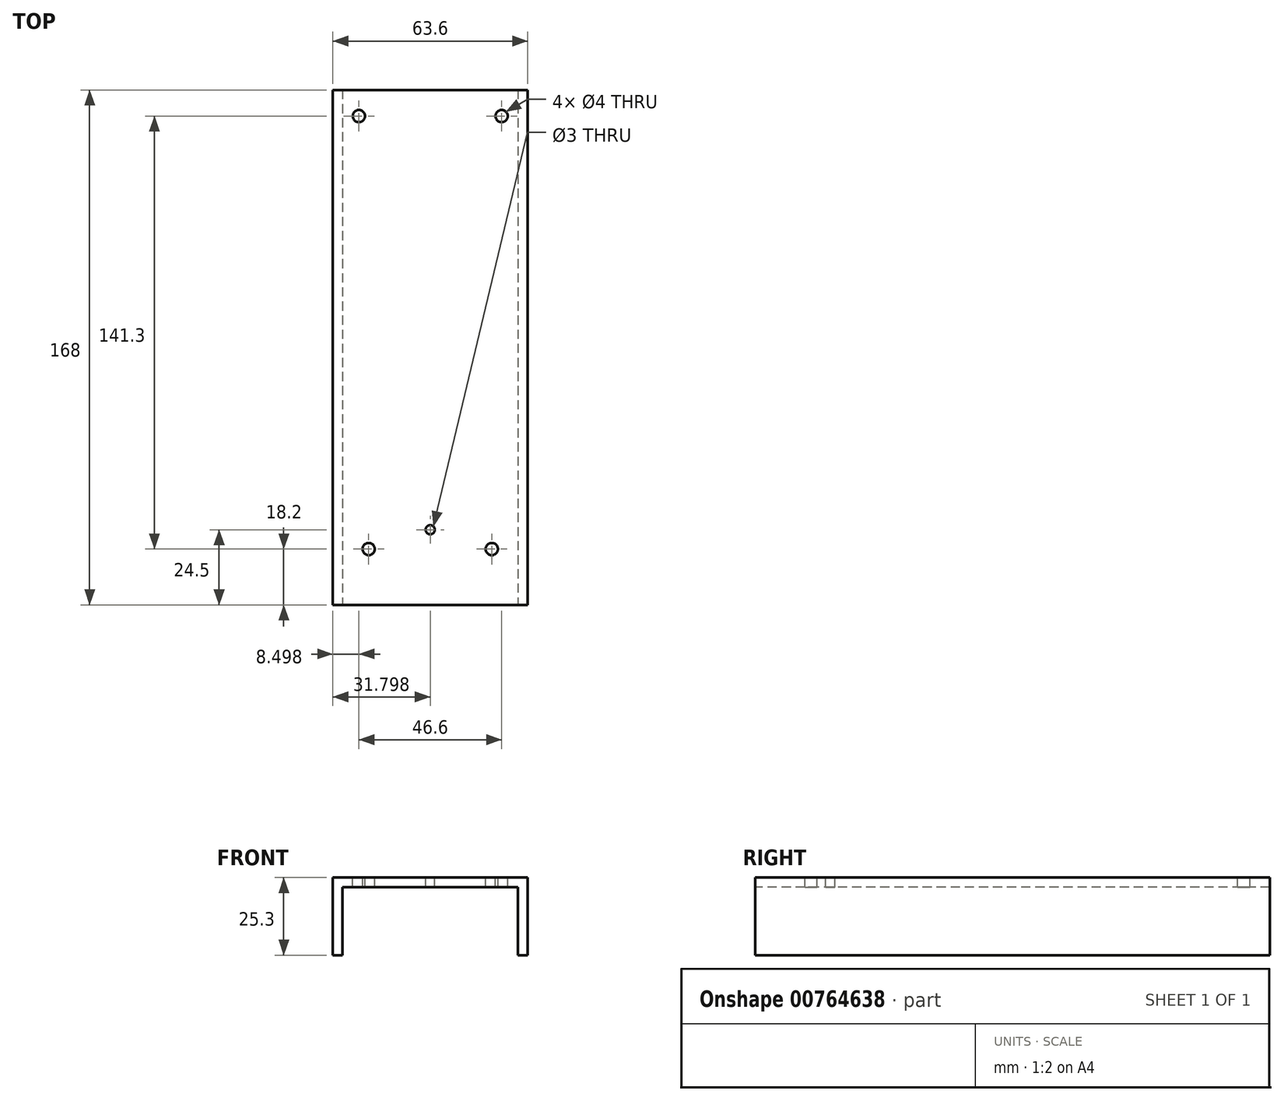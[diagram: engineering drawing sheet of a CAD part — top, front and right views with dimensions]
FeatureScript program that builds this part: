
annotation { "Feature Type Name" : "Feature", "Feature Type Description" : "" }
export const myFeature = defineFeature(function(context is Context, id is Id, definition is map)
    precondition{}
    {
        {
            var Q0;
            Q0=qCreatedBy(makeId("Front.planeOp"),FACE);
            var sketch = newSketch(context, id + "F0", { "sketchPlane" : qUnion([Q0])});
            skLineSegment(sketch, "E0.bottom", {"start": v(-38.46, -26.03) * mm, "end": v(-35.31, -26.03) * mm});
            skLineSegment(sketch, "E0.left", {"start": v(-38.46, -26.03) * mm, "end": v(-38.46, -0.73) * mm});
            skLineSegment(sketch, "E0.right", {"start": v(-35.31, -26.03) * mm, "end": v(-35.31, -3.88) * mm});
            skLineSegment(sketch, "E1.top", {"start": v(-35.31, -3.88) * mm, "end": v(21.99, -3.88) * mm});
            skLineSegment(sketch, "E2.top", {"start": v(25.14, -26.03) * mm, "end": v(21.99, -26.03) * mm});
            skLineSegment(sketch, "E2.right", {"start": v(21.99, -3.88) * mm, "end": v(21.99, -26.03) * mm});
            skPoint(sketch, "E3", {"position": v(-38.46, -0.73) * mm});
            skPoint(sketch, "E4", {"position": v(25.14, -0.73) * mm});
            skLineSegment(sketch, "E5", {"start": v(-38.46, -0.73) * mm, "end": v(25.14, -0.73) * mm});
            skLineSegment(sketch, "E6", {"start": v(25.14, -0.73) * mm, "end": v(25.14, -26.03) * mm});
            skSolve(sketch);
        }
        {
            var Q0;
            Q0=makeQuery(id+"F0.imprint","IMPRINT",FACE,{"disambiguationData":[TD([[makeQuery(id+"F0.imprint","IMPRINT",EDGE,{"derivedFrom":sQuery(id+"F0.wireOp",EDGE,"E0.bottom")}),1.0]])]});
            extrude(context, id + "F1", {"entities" : qUnion([Q0]), "oppositeDirection" : true, "depth" : 168 * mm, "offsetDistance" : 25 * mm});
        }
        {
            var Q0;
            Q0=makeQuery(id+"F1.opExtrude","SWEPT_FACE",FACE,{"disambiguationData":[OSD([sQuery(id+"F0.wireOp",EDGE,"E5")])]});
            var sketch = newSketch(context, id + "F2", { "sketchPlane" : qUnion([Q0])});
            skCircle(sketch, "E7", {"center": v(-29.96, 159.5) * mm, "radius": 2 * mm});
            skCircle(sketch, "E8", {"center": v(16.64, 159.5) * mm, "radius": 2 * mm});
            skCircle(sketch, "E9", {"center": v(-6.66, 24.5) * mm, "radius": 1.5 * mm});
            skPoint(sketch, "E9.centerSnap0", {"position": v(-6.66, 0) * mm});
            skCircle(sketch, "E10", {"center": v(13.44, 18.2) * mm, "radius": 2 * mm});
            skCircle(sketch, "E11", {"center": v(-26.76, 18.2) * mm, "radius": 2 * mm});
            skSolve(sketch);
        }
        {
            var Q0;
            Q0 = qSketchRegion(id + "F2", true);
            extrude(context, id + "F3", {"entities" : qUnion([Q0]), "operationType" : NewBodyOperationType.REMOVE, "oppositeDirection" : true, "depth" : 3.15 * mm, "offsetDistance" : 25 * mm});
        }
    });
